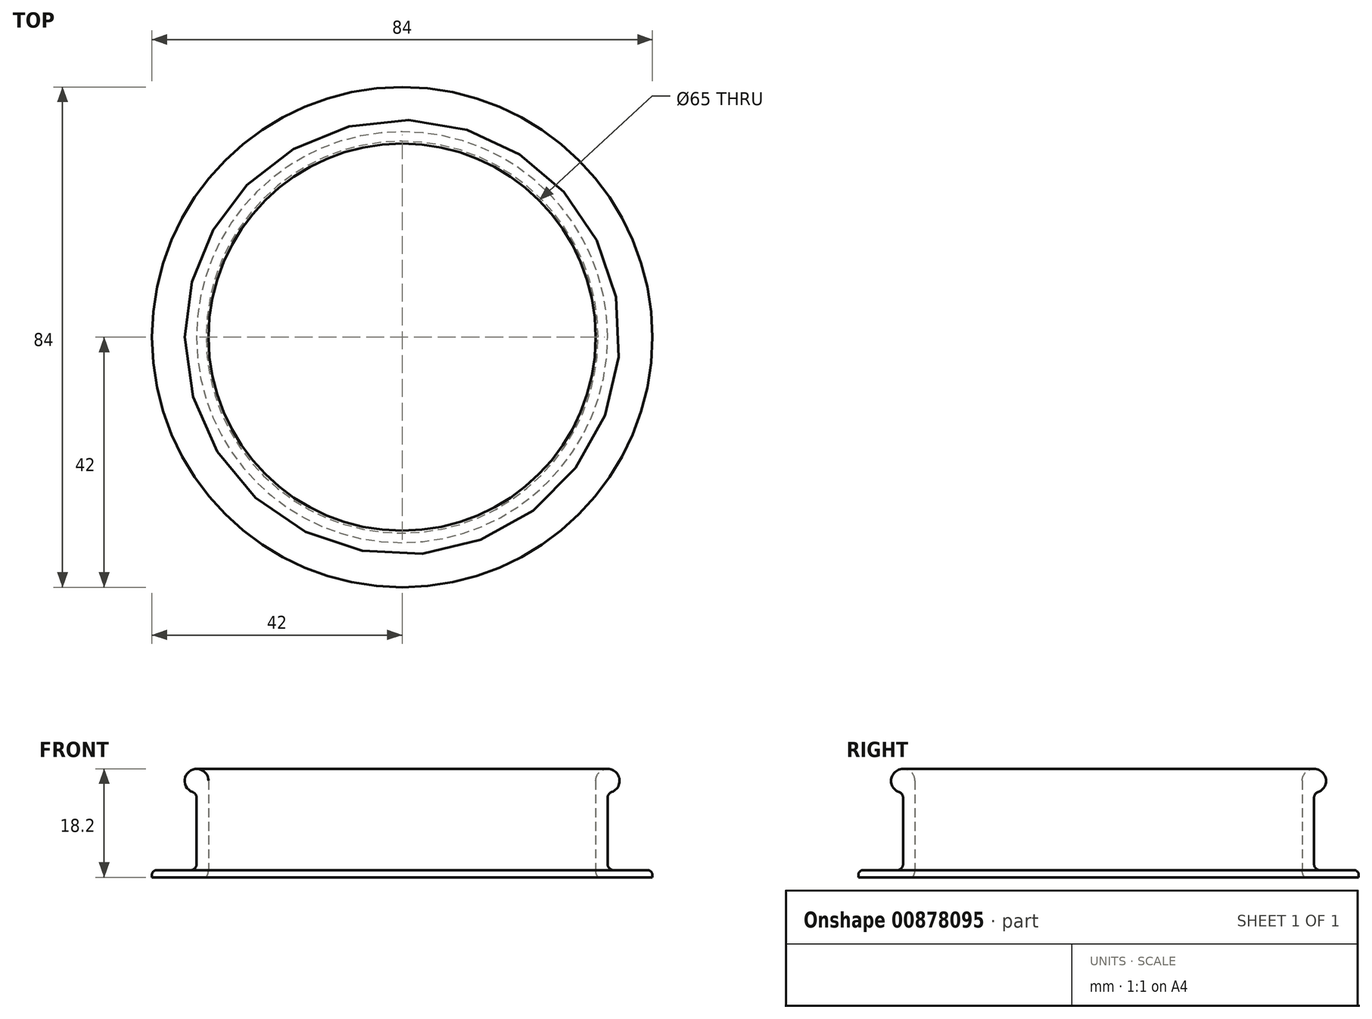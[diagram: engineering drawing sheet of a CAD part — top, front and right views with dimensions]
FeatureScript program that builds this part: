
annotation { "Feature Type Name" : "Feature", "Feature Type Description" : "" }
export const myFeature = defineFeature(function(context is Context, id is Id, definition is map)
    precondition{}
    {
        {
            var Q0;
            Q0=qCreatedBy(makeId("Top.planeOp"),FACE);
            var sketch = newSketch(context, id + "F0", { "sketchPlane" : qUnion([Q0])});
            skCircle(sketch, "E0", {"center": v(0, 0) * mm, "radius": 42 * mm});
            skCircle(sketch, "E1", {"center": v(0, 0) * mm, "radius": 36.5 * mm});
            skSolve(sketch);
        }
        {
            var Q0;
            Q0=qSketchRegion(id+"F0",true);
            extrude(context, id + "F1", {"entities" : qUnion([Q0]), "depth" : 2 * mm, "offsetDistance" : 25 * mm});
        }
        {
            var Q0;
            Q0=qCreatedBy(makeId("Front.planeOp"),FACE);
            var sketch = newSketch(context, id + "F2", { "sketchPlane" : qUnion([Q0])});
            skLineSegment(sketch, "E2", {"start": v(0, 0) * mm, "end": v(0, 127.1) * mm, "construction": true});
            skLineSegment(sketch, "E3.0", {"start": v(-36.5, 0) * mm, "end": v(0, 0) * mm});
            skLineSegment(sketch, "E4.0", {"start": v(-36.5, 2) * mm, "end": v(0, 2) * mm});
            skLineSegment(sketch, "E5", {"start": v(36.5, 2) * mm, "end": v(36.5, 0) * mm});
            skLineSegment(sketch, "E6", {"start": v(34.5, 3) * mm, "end": v(34.5, 14.17) * mm});
            skLineSegment(sketch, "E7", {"start": v(32.5, 2) * mm, "end": v(32.5, 17) * mm});
            skLineSegment(sketch, "E8.trimOffspring", {"start": v(35.5, 2) * mm, "end": v(36.5, 2) * mm});
            skLineSegment(sketch, "E9.trimOffspring", {"start": v(34.5, 0) * mm, "end": v(36.5, 0) * mm});
            skArc(sketch, "E10", {"start": v(35.17, 15.11) * mm, "mid": v(35.65, 18.63) * mm, "end": v(32.5, 17) * mm});
            skPoint(sketch, "E11.visualSharp", {"position": v(34.5, 2) * mm});
            skArc(sketch, "E11.filletArc", {"start": v(34.5, 3) * mm, "mid": v(34.8, 2.3) * mm, "end": v(35.5, 2) * mm});
            skPoint(sketch, "E12.visualSharp", {"position": v(32.5, 0) * mm});
            skArc(sketch, "E12.filletArc", {"start": v(32.5, 2) * mm, "mid": v(33.09, 0.59) * mm, "end": v(34.5, 0) * mm});
            skPoint(sketch, "E13.visualSharp", {"position": v(34.5, 15) * mm});
            skArc(sketch, "E13.filletArc", {"start": v(35.17, 15.11) * mm, "mid": v(34.68, 14.75) * mm, "end": v(34.5, 14.17) * mm});
            skSolve(sketch);
        }
        {
            var Q0;
            Q0=qSketchRegion(id+"F2",true);
            var Q1;
            Q1=sQuery(id+"F2.wireOp",EDGE,"E2");
            revolve(context, id + "F3", {"operationType" : NewBodyOperationType.ADD, "surfaceOperationType" : NewSurfaceOperationType.NEW, "entities" : qUnion([Q0]), "axis" : qUnion([Q1]), "revolveType" : RevolveType.FULL});
        }
        {
            var Q0;
            Q0=qCreatedBy(makeId("Top.planeOp"),FACE);
            var sketch = newSketch(context, id + "F4", { "sketchPlane" : qUnion([Q0])});
            skLineSegment(sketch, "E14.bottom", {"start": v(-64.74, -78.41) * mm, "end": v(69.62, -78.41) * mm});
            skLineSegment(sketch, "E14.top", {"start": v(-64.74, 74.62) * mm, "end": v(69.62, 74.62) * mm});
            skLineSegment(sketch, "E14.left", {"start": v(-64.74, -78.41) * mm, "end": v(-64.74, 74.62) * mm});
            skLineSegment(sketch, "E14.right", {"start": v(69.62, -78.41) * mm, "end": v(69.62, 74.62) * mm});
            skSolve(sketch);
        }
        {
            var Q0;
            Q0 = qSketchRegion(id + "F4", true);
            extrude(context, id + "F5", {"entities" : qUnion([Q0]), "operationType" : NewBodyOperationType.REMOVE, "depth" : 0.8 * mm, "offsetDistance" : 25 * mm});
        }
        {
            var Q0;
            Q0=makeQuery(id+"F1.opExtrude","CAP_EDGE",EDGE,{"disambiguationData":[OSD([sQuery(id+"F0.wireOp",EDGE,"E0")])],"isStart":false});
            fillet(context, id + "F6", {"entities" : qUnion([Q0]), "radius" : 0.8 * mm, "tangentPropagation" : true, "allowEdgeOverflow" : false});
        }
    });
